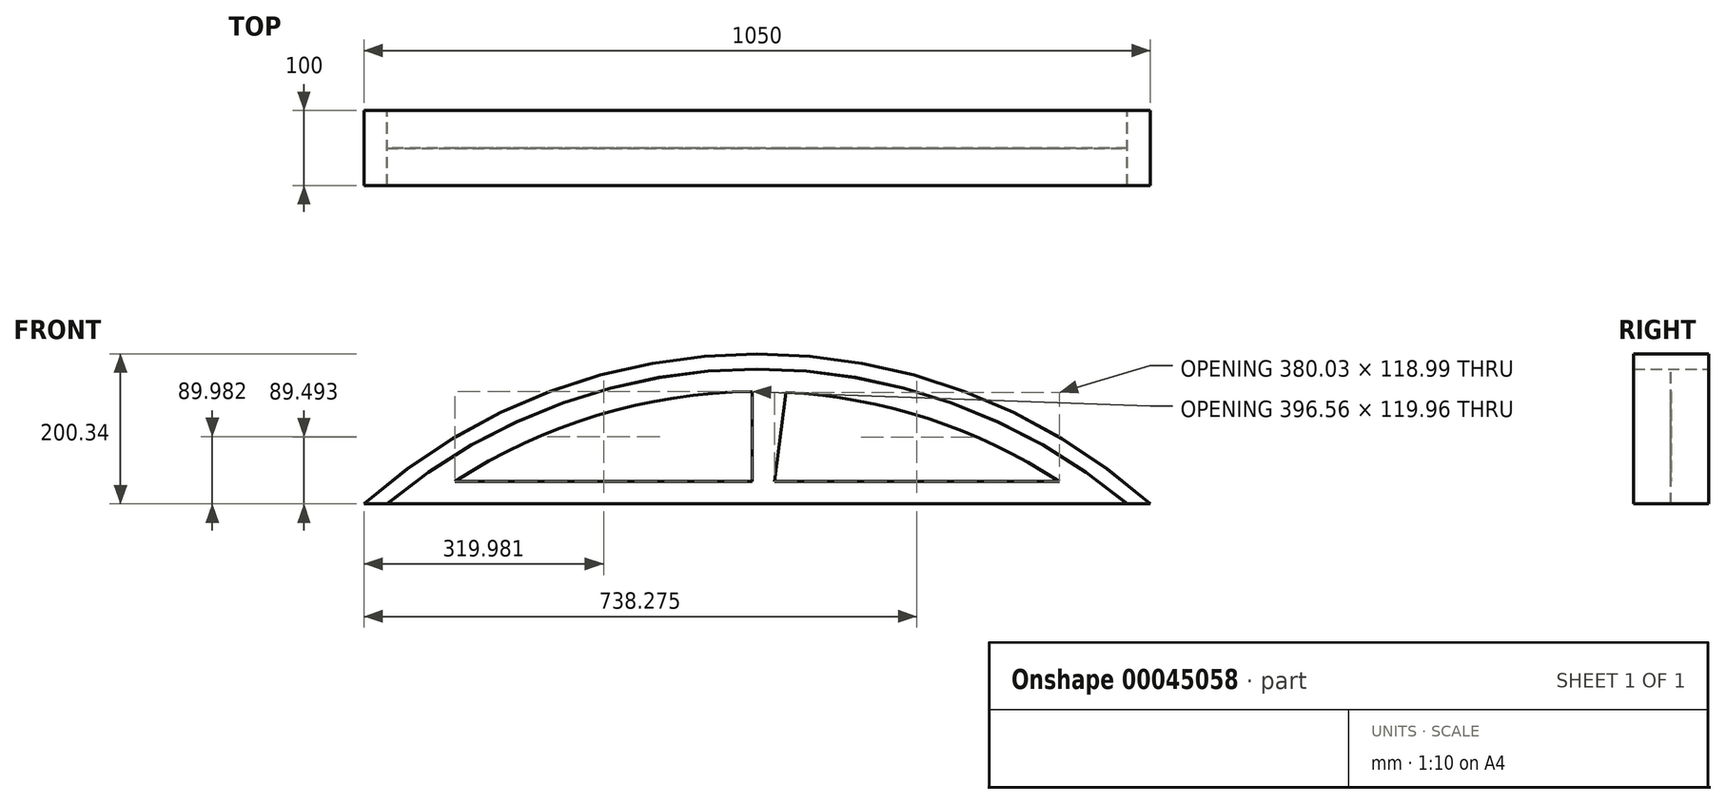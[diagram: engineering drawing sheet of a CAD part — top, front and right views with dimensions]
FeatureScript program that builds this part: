
annotation { "Feature Type Name" : "Feature", "Feature Type Description" : "" }
export const myFeature = defineFeature(function(context is Context, id is Id, definition is map)
    precondition{}
    {
        {
            var Q0;
            Q0=qCreatedBy(makeId("Front.planeOp"),FACE);
            var sketch = newSketch(context, id + "F0", { "sketchPlane" : qUnion([Q0])});
            skLineSegment(sketch, "E0", {"start": v(-501.9, 0) * mm, "end": v(548.1, 0) * mm, "construction": true});
            skLineSegment(sketch, "E1", {"start": v(0, 0) * mm, "end": v(0, 200) * mm, "construction": true});
            skArc(sketch, "E2", {"start": v(548.1, 0) * mm, "mid": v(23.1, 200.34) * mm, "end": v(-501.9, 0) * mm});
            skArc(sketch, "E3", {"start": v(547.9, 0) * mm, "mid": v(23.1, 200.2) * mm, "end": v(-501.68, 0) * mm});
            skLineSegment(sketch, "E4", {"start": v(-501.9, 0) * mm, "end": v(-501.68, 0) * mm});
            skLineSegment(sketch, "E5", {"start": v(548.1, 0) * mm, "end": v(547.9, 0) * mm});
            skSolve(sketch);
        }
        {
            var Q0;
            Q0=makeQuery(id+"F0.imprint","IMPRINT",FACE,{"disambiguationData":[TD([[makeQuery(id+"F0.imprint","IMPRINT",EDGE,{"derivedFrom":sQuery(id+"F0.wireOp",EDGE,"E2")}),1.0]])]});
            extrude(context, id + "F1", {"entities" : qUnion([Q0]), "depth" : 100 * mm});
        }
        {
            var Q0;
            Q0=qCreatedBy(makeId("Front.planeOp"),FACE);
            var sketch = newSketch(context, id + "F2", { "sketchPlane" : qUnion([Q0])});
            skLineSegment(sketch, "E6", {"start": v(-501.68, 0) * mm, "end": v(547.9, 0) * mm, "construction": true});
            skLineSegment(sketch, "E7", {"start": v(0, 0) * mm, "end": v(0, 199.86) * mm, "construction": true});
            skArc(sketch, "E8", {"start": v(547.9, 0) * mm, "mid": v(23.1, 200.2) * mm, "end": v(-501.68, 0) * mm});
            skArc(sketch, "E9", {"start": v(517.35, 0) * mm, "mid": v(23.1, 180.2) * mm, "end": v(-471.14, 0) * mm});
            skLineSegment(sketch, "E10", {"start": v(-501.68, 0) * mm, "end": v(-471.14, 0) * mm});
            skLineSegment(sketch, "E11", {"start": v(517.35, 0) * mm, "end": v(547.9, 0) * mm});
            skSolve(sketch);
        }
        {
            var Q0;
            Q0=makeQuery(id+"F2.imprint","IMPRINT",FACE,{"disambiguationData":[TD([[makeQuery(id+"F2.imprint","IMPRINT",EDGE,{"derivedFrom":sQuery(id+"F2.wireOp",EDGE,"E8")}),1.0]])]});
            extrude(context, id + "F3", {"entities" : qUnion([Q0]), "depth" : 100 * mm});
        }
        {
            var Q0;
            Q0=qCreatedBy(makeId("Front.planeOp"),FACE);
            var sketch = newSketch(context, id + "F4", { "sketchPlane" : qUnion([Q0])});
            skLineSegment(sketch, "E12", {"start": v(-471.14, 0) * mm, "end": v(517.35, 0) * mm, "construction": true});
            skLineSegment(sketch, "E13", {"start": v(0, 0) * mm, "end": v(0, 179.85) * mm, "construction": true});
            skArc(sketch, "E14", {"start": v(517.35, 0) * mm, "mid": v(23.1, 180.2) * mm, "end": v(-471.14, 0) * mm});
            skArc(sketch, "E15", {"start": v(517.04, 0) * mm, "mid": v(23.1, 180) * mm, "end": v(-470.83, 0) * mm});
            skLineSegment(sketch, "E16", {"start": v(-471.14, 0) * mm, "end": v(-470.83, 0) * mm});
            skLineSegment(sketch, "E17", {"start": v(517.04, 0) * mm, "end": v(517.35, 0) * mm});
            skSolve(sketch);
        }
        {
            var Q0;
            Q0 = qSketchRegion(id + "F4", true);
            extrude(context, id + "F5", {"entities" : qUnion([Q0]), "depth" : 100 * mm});
        }
        {
            var Q0;
            Q0=qCreatedBy(makeId("Front.planeOp"),FACE);
            var sketch = newSketch(context, id + "F6", { "sketchPlane" : qUnion([Q0])});
            skLineSegment(sketch, "E18", {"start": v(-470.83, 0) * mm, "end": v(517.04, 0) * mm});
            skLineSegment(sketch, "E19", {"start": v(0, 0) * mm, "end": v(23.1, 180) * mm, "construction": true});
            skPoint(sketch, "E19.endSnap0", {"position": v(23.1, 0) * mm});
            skArc(sketch, "E20", {"start": v(517.04, 0) * mm, "mid": v(23.1, 180) * mm, "end": v(-470.83, 0) * mm});
            skLineSegment(sketch, "E21", {"start": v(-380.19, 30) * mm, "end": v(16.37, 30) * mm});
            skArc(sketch, "E22", {"start": v(426.4, 30) * mm, "mid": v(251.9, 113.62) * mm, "end": v(61.64, 148.99) * mm});
            skLineSegment(sketch, "E23", {"start": v(16.37, 149.96) * mm, "end": v(16.37, 30) * mm});
            skLineSegment(sketch, "E24", {"start": v(61.64, 148.99) * mm, "end": v(46.37, 30) * mm});
            skArc(sketch, "E25.trimOffspring", {"start": v(16.37, 149.96) * mm, "mid": v(-190.5, 118.4) * mm, "end": v(-380.19, 30) * mm});
            skLineSegment(sketch, "E26.trimOffspring", {"start": v(46.37, 30) * mm, "end": v(426.4, 30) * mm});
            skSolve(sketch);
        }
        {
            var Q0;
            Q0=makeQuery(id+"F6.imprint","IMPRINT",FACE,{"disambiguationData":[TD([[makeQuery(id+"F6.imprint","IMPRINT",EDGE,{"derivedFrom":sQuery(id+"F6.wireOp",EDGE,"E18")}),1.0]])]});
            extrude(context, id + "F7", {"entities" : qUnion([Q0]), "depth" : 50.57 * mm, "hasSecondDirection" : true, "secondDirectionOppositeDirection" : false, "secondDirectionDepth" : 50 * mm});
        }
    });
